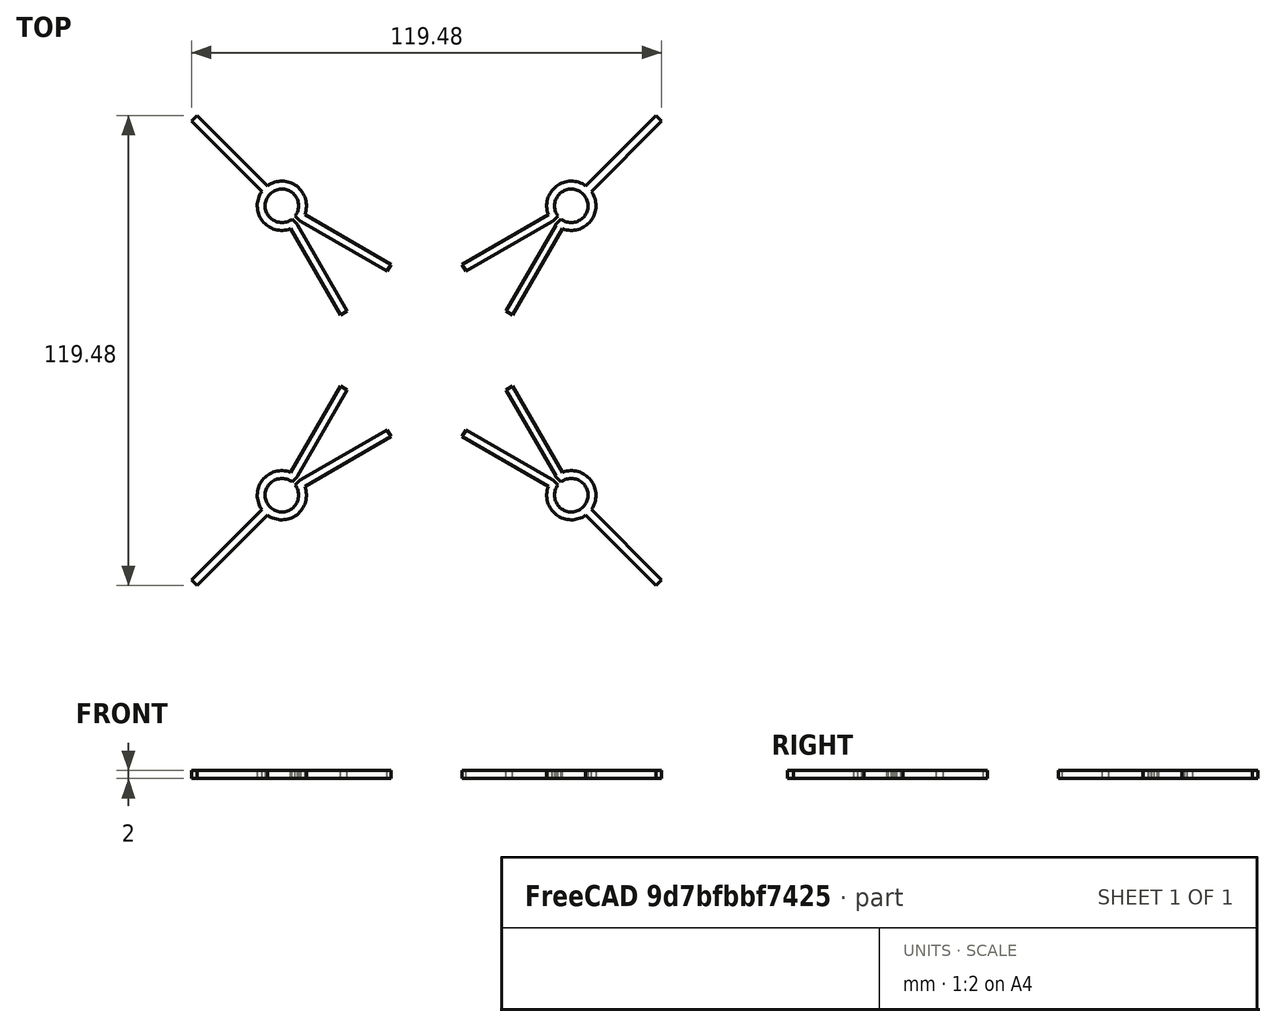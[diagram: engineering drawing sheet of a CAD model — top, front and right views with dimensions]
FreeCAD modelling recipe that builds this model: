
FCSTD DOCUMENT  (FreeCAD 0.19R23578 (Git))
Label: brace
License: All rights reserved
LicenseURL: http://en.wikipedia.org/wiki/All_rights_reserved
objects: Part::Feature×4, Part::Extrusion×4
note: 8 computed .brp shape members not serialized (recipe doc carries the construction recipe); baked Part::Feature solids carry a one-line shape summary decoded from their .brp

FEATURE [Part::Feature] Face
  shape: bbox 50.74 x 50.74 x 2e-07 mm, 1 faces, 0 solids (baked)
FEATURE [Part::Feature] Face001
  shape: bbox 50.74 x 50.74 x 2e-07 mm, 1 faces, 0 solids (baked)
FEATURE [Part::Feature] Face002
  shape: bbox 50.74 x 50.74 x 2e-07 mm, 1 faces, 0 solids (baked)
FEATURE [Part::Feature] Face003
  shape: bbox 50.74 x 50.74 x 2e-07 mm, 1 faces, 0 solids (baked)
FEATURE [Part::Extrusion] Extrude
  Base = -> Face
  Dir = (0,0,1)
  DirMode = 0
  FaceMakerClass = Part::FaceMakerBullseye
  LengthFwd = 2
  LengthRev = 0
  Solid = false
  Symmetric = false
FEATURE [Part::Extrusion] Extrude001
  Base = -> Face001
  Dir = (0,0,1)
  DirMode = 0
  FaceMakerClass = Part::FaceMakerBullseye
  LengthFwd = 2
  LengthRev = 0
  Solid = false
  Symmetric = false
FEATURE [Part::Extrusion] Extrude002
  Base = -> Face002
  Dir = (0,0,1)
  DirMode = 0
  FaceMakerClass = Part::FaceMakerBullseye
  LengthFwd = 2
  LengthRev = 0
  Solid = false
  Symmetric = false
FEATURE [Part::Extrusion] Extrude003
  Base = -> Face003
  Dir = (0,0,1)
  DirMode = 0
  FaceMakerClass = Part::FaceMakerBullseye
  LengthFwd = 2
  LengthRev = 0
  Solid = false
  Symmetric = false
